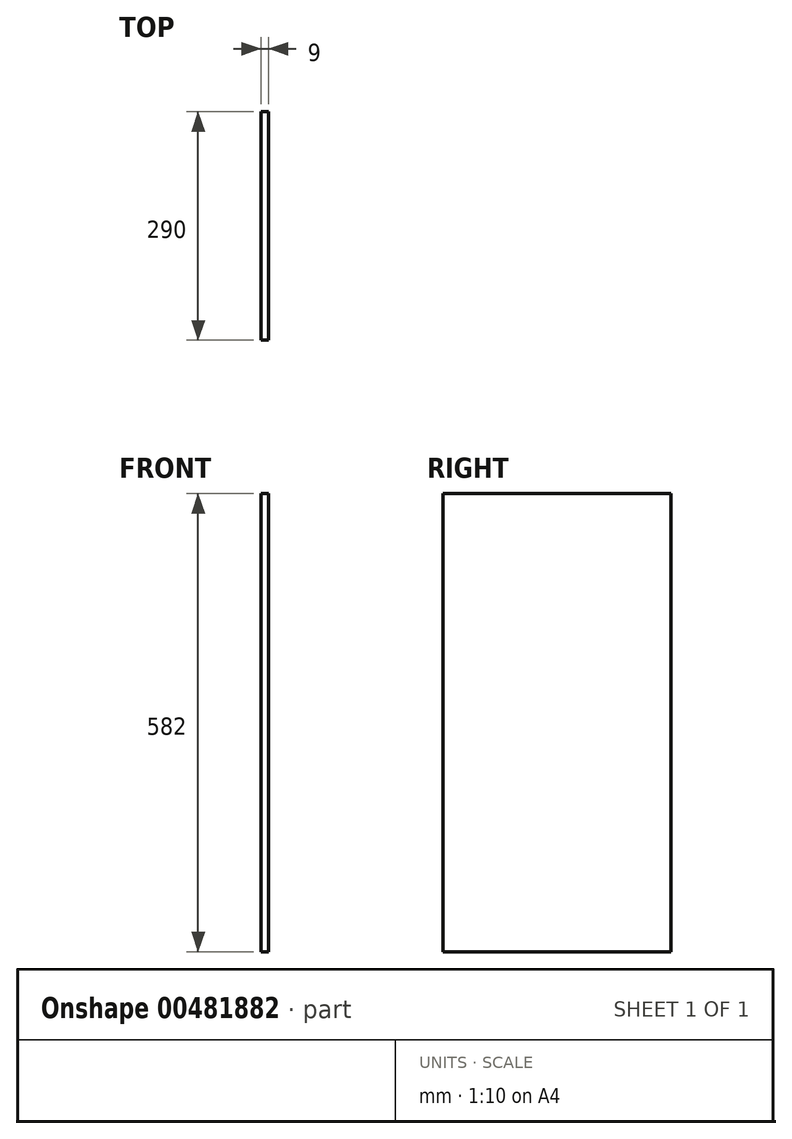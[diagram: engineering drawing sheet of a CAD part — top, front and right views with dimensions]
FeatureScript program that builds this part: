
annotation { "Feature Type Name" : "Feature", "Feature Type Description" : "" }
export const myFeature = defineFeature(function(context is Context, id is Id, definition is map)
    precondition{}
    {
        {
            var Q0;
            Q0=qCreatedBy(makeId("Right.planeOp"),FACE);
            var sketch = newSketch(context, id + "F0", { "sketchPlane" : qUnion([Q0])});
            skLineSegment(sketch, "E0.bottom", {"start": v(0, 0) * mm, "end": v(-290, 0) * mm});
            skLineSegment(sketch, "E0.top", {"start": v(0, 582) * mm, "end": v(-290, 582) * mm});
            skLineSegment(sketch, "E0.left", {"start": v(0, 0) * mm, "end": v(0, 582) * mm});
            skLineSegment(sketch, "E0.right", {"start": v(-290, 0) * mm, "end": v(-290, 582) * mm});
            skSolve(sketch);
        }
        {
            var Q0;
            Q0 = qSketchRegion(id + "F0", true);
            extrude(context, id + "F1", {"entities" : qUnion([Q0]), "depth" : 9 * mm});
        }
    });
